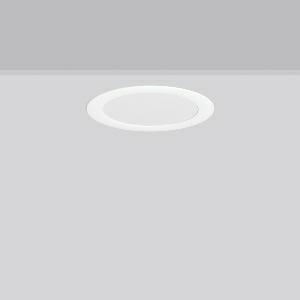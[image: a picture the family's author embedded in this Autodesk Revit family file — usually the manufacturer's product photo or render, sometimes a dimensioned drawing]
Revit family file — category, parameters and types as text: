
# Revit family: toledo_flat_round_e_672224_002_04_aff2
name_source: partatom
category: Lighting Fixtures
units: mm (PartAtom-declared; Revit-internal decimal feet)

## family parameters
Cut with Voids When Loaded = No
Host = Face
Light Source = No
Part Type = Normal
Room Calculation Point = No
Round Connector Dimension = Use Diameter
Shared = No

## types (1)
- TOLEDO FLAT round E (1 x LED Modul 830, 1650 lm, 3000)
    Apparent Load = 17 VA
    CIE Flux Codes = 48 79 96 100 100
    Color Rendering = 80
    Color Temperature = 3000
    Default Elevation = 1800 mm
    Description = Series: TOLEDO FLAT round
Ultra thin recessed downlight. For escape route illumination. Housing: die-cast aluminium, powder-coated. Lightguide and diffuser made of non-yellowing plastic (PMMA). Diffuser opal matt plastic. Ceiling installation with spring system. Including separate LED converter with connecting cable 250 mm. Self-contained system with automatic self-test and feedback to the RZB monitoring system MULTIDIGIT. External driver with simple plug-in locking system. 
Colour: white
Diameter: 255 mm
Height: 3 mm
Cut-out diameter: 234 mm
Recess height: 100 mm
Luminaire: recess height: 60-80 mm
Weight: 1.77 kg
Operating mode: maintained power mode
Duration time: 3 h
Lamp: LED
Socket: without socket
Colour temperature: 3000K
Colour rendering index (CRI): 80
System power: 17 W
Rated luminous flux: 1650 lm
Luminous flux, emergency: 450 lm
System power, emergency: -
Control gear: Regulated power supply
Protection class: I
Type of protection: IP 54
    Height = 0 mm  [stored 0 ft]
    Lamp = 1 x LED Modul 830
    Lamp Light Flux = 1650 lm
    Lamp count = 1
    Length = 255 mm
    Lifetime = 50000 h
    Luminous efficacy = 97 lm/W
    Manufacturer = RZB
    ModVariant = No
    Model = 672224.002.04
    Mounting Place = Ceiling
    Mounting Type = Recessed
    Number of Poles = 1
    OnlyDefault = Yes
    Power Factor = 1
    Product Name = TOLEDO FLAT round E
    Product group = Recessed downlights
    ProductGroupID = 402
    Protection Class = Protection class I
    Protection Degree = IP 40
    RLX_Detail_Level = 1
    RLX_Emergency_Light_Flux = 450 lm
    RLX_Emergency_Type = 3
    RLX_Emergency_Type_DB = Yes
    RlxData = <blob elided: 30349 chars, md5=38d5678b>
    Socket = socket
    Standby Power = 0 W
    System Light Flux = 1650 lm
    System Power = 17 W
    Type Comments = Product without accessories
    Type Image = 901453.002.jpg
    URL = http://relux.com
    VarID = ---
    Voltage = 0 V
    Weight = 0.00 kg
    Width = 0 mm  [stored 0 ft]

note: [stored X ft] marks values corroborated as IEEE doubles in the binary element streams (Revit-internal decimal feet)

## geometry (parser evidence)
native form markers: Blend x4, Sweep x11
no freeform markers — native parametric forms only
